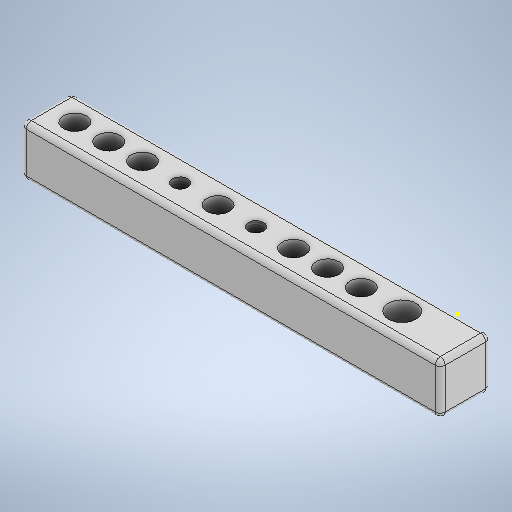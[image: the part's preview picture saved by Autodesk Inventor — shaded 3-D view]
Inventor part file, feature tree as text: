
AUTODESK INVENTOR PART (.ipt)
format: ipt  version: 2025.2 (Build 292293000, 293)  size: 436,736 bytes
history: native  units: in
note: dims shown in document units (in); Inventor stores cm internally (conversion verified against a paired STEP export)
features: sketch x19, extrude x15, thread x4, fillet x3
ambient origin geometry x8: Origin, YZ Plane, XZ Plane, XY Plane, X Axis, Y Axis, Z Axis, Center Point
bodies: Solid1 (feature_tree)
feature tree (41):
  extrude  "Extrusion1"  Depth=0.3937in
  sketch  "Sketch2"  dims[d8=0.1181in d9=0.1181in]
  extrude  "Extrusion2"  Depth=0.3937in
  extrude  "Extrusion3"  Depth=0.1181in
  extrude  "Extrusion4"  Depth=0.3937in TaperAngle=0.0deg
  extrude  "Extrusion5"  Depth=0.3937in
  thread  "Thread1"  [1 undecoded]
  thread  "Thread2"  [1 undecoded]
  extrude  "Extrusion6"  Depth=0.3937in TaperAngle=0.0deg
  extrude  "Extrusion7"  Depth=0.3937in TaperAngle=0.0deg
  extrude  "Extrusion8"  Depth=0.0394in
  sketch  "Sketch7"  dims[d61=0.5906in d62=0.5906in]
  fillet  "Fillet3"  Radius=0.0394in
  fillet  "Fillet4"  Radius=0.1969in
  sketch  "Sketch8"  dims[d63=0.1181in d64=0.1181in]
  extrude  "Extrusion9"  Depth=0.3937in
  extrude  "Extrusion10"  Depth=0.3937in TaperAngle=0.0deg
  extrude  "Extrusion11"  Depth=0.5906in
  extrude  "Extrusion12"  Depth=0.1181in
  extrude  "Extrusion13"  Depth=0.3937in
  extrude  "Extrusion14"  Depth=0.1457in
  thread  "Thread3"  [1 undecoded]
  thread  "Thread4"  [1 undecoded]
  fillet  "Fillet5"  Radius=0.3937in
  extrude  "Extrusion15"  Depth=0.3937in TaperAngle=0.0deg
  sketch  "Sketch1"  dims[d0=6.6929in d1=0.3937in]
  sketch  "Sketch3"  dims[d14=0.3937in d15=0.0in d18=2.7559in d20=0.3937in d21=0.3937in d23=0.3937in d30=2.3622in d32=0.3937in d33=0.3937in d35=0.3937in d37=0.3937in d38=0.0in]
  sketch  "Sketch Rectangular Pattern1"  dims[d2=0.3937in d3=0.0in d4=0.0866in]
  sketch  "Sketch Rectangular Pattern2"  dims[d10=0.3937in d11=0.0in d12=0.3937in d13=0.0in]
  sketch  "Sketch4"  dims[d39=0.3937in d40=0.0in d41=0.3937in d42=0.0in]
  sketch  "Sketch5"  dims[d49=0.3937in d50=0.0in d51=0.0394in d52=0.0394in d53=0.1969in]
  sketch  "Sketch6"  dims[d57=0.3937in d58=0.0in d59=0.3937in d60=0.0in]
  sketch  "Sketch9"  dims[d65=0.3937in d66=0.0in d67=0.1772in]
  sketch  "Sketch10"  dims[d68=0.1457in d69=0.1457in d71=0.1772in d73=0.1772in]
  sketch  "Sketch11"  dims[d81=1.1811in d83=0.2638in d84=0.3937in d86=0.3937in]
  sketch  "Sketch12"  dims[d88=1.1811in d90=0.2638in d91=0.3937in d93=0.3937in d95=0.3937in d96=0.0in]
  sketch  "Sketch13"  dims[d97=0.1772in d98=0.3937in d99=0.0in]
  sketch  "Sketch Rectangular Pattern4"  dims[d44=0.3937in d45=0.0in d46=0.3937in d47=0.0in]
  sketch  "Sketch Rectangular Pattern5"  dims[d54=0.3937in d55=0.0in d56=0.1969in]
  sketch  "Sketch14"  dims[d100=0.3937in d101=0.0in]
  sketch  "Sketch15"  dims[d102=0.3937in d103=0.0in d104=0.0394in d105=0.2165in d106=0.3937in d107=0.0in]
note: 4 required parameter values undecoded (feature->parameter linkage not recoverable at this tier; creation-order binding heuristic only, values carry confidence <= 0.55)
